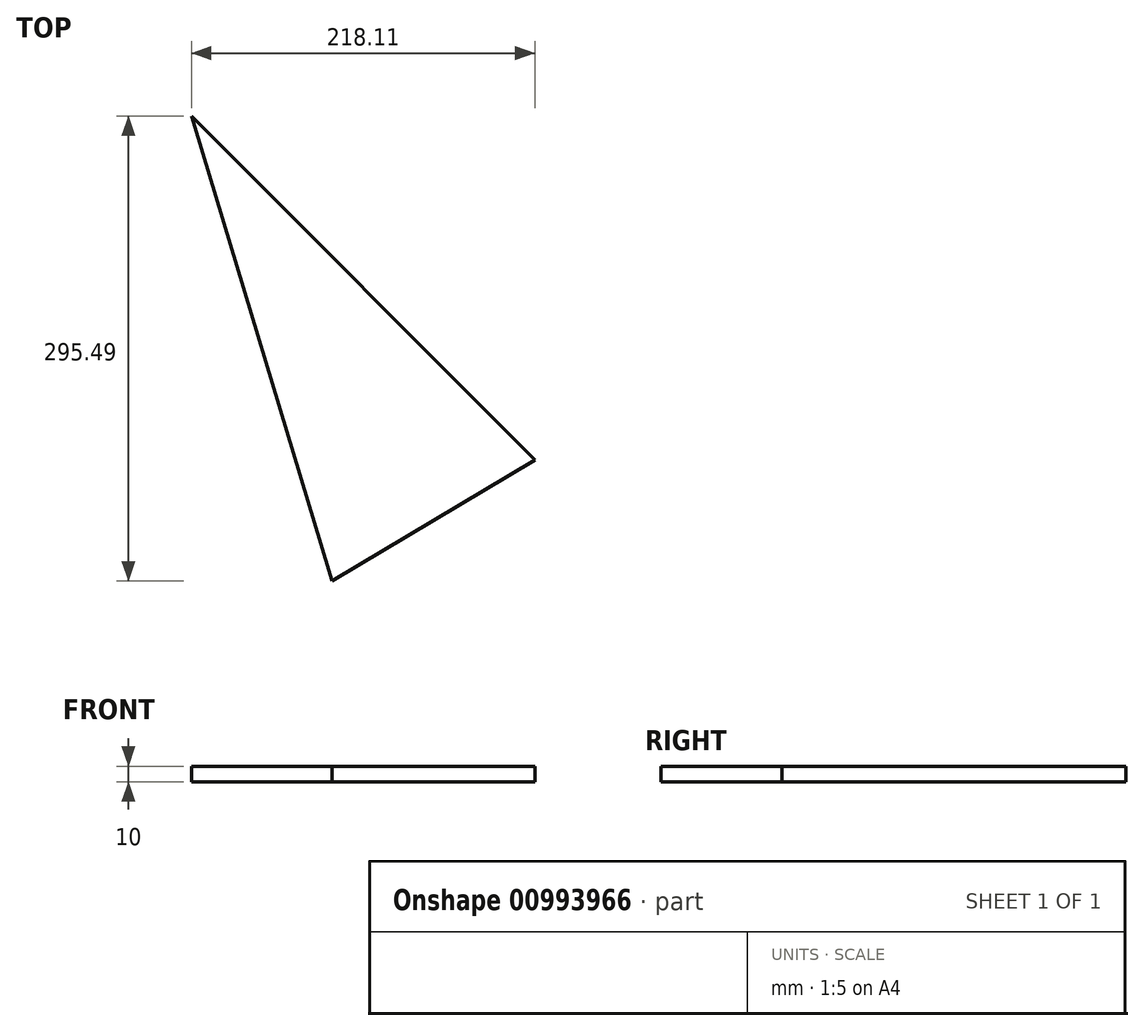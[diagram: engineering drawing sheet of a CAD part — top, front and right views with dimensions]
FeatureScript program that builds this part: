
annotation { "Feature Type Name" : "Feature", "Feature Type Description" : "" }
export const myFeature = defineFeature(function(context is Context, id is Id, definition is map)
    precondition{}
    {
        {
            var Q0;
            Q0=qCreatedBy(makeId("Top.planeOp"),FACE);
            var sketch = newSketch(context, id + "F0", { "sketchPlane" : qUnion([Q0])});
            skLineSegment(sketch, "E0", {"start": v(-40.56, -145.95) * mm, "end": v(-129.94, 149.54) * mm});
            skLineSegment(sketch, "E1", {"start": v(-129.94, 149.54) * mm, "end": v(88.17, -68.94) * mm});
            skLineSegment(sketch, "E2", {"start": v(88.17, -68.94) * mm, "end": v(-40.56, -145.95) * mm});
            skSolve(sketch);
        }
        {
            var Q0;
            Q0 = qSketchRegion(id + "F0", true);
            extrude(context, id + "F1", {"entities" : qUnion([Q0]), "depth" : 10 * mm, "offsetDistance" : 25 * mm});
        }
    });
